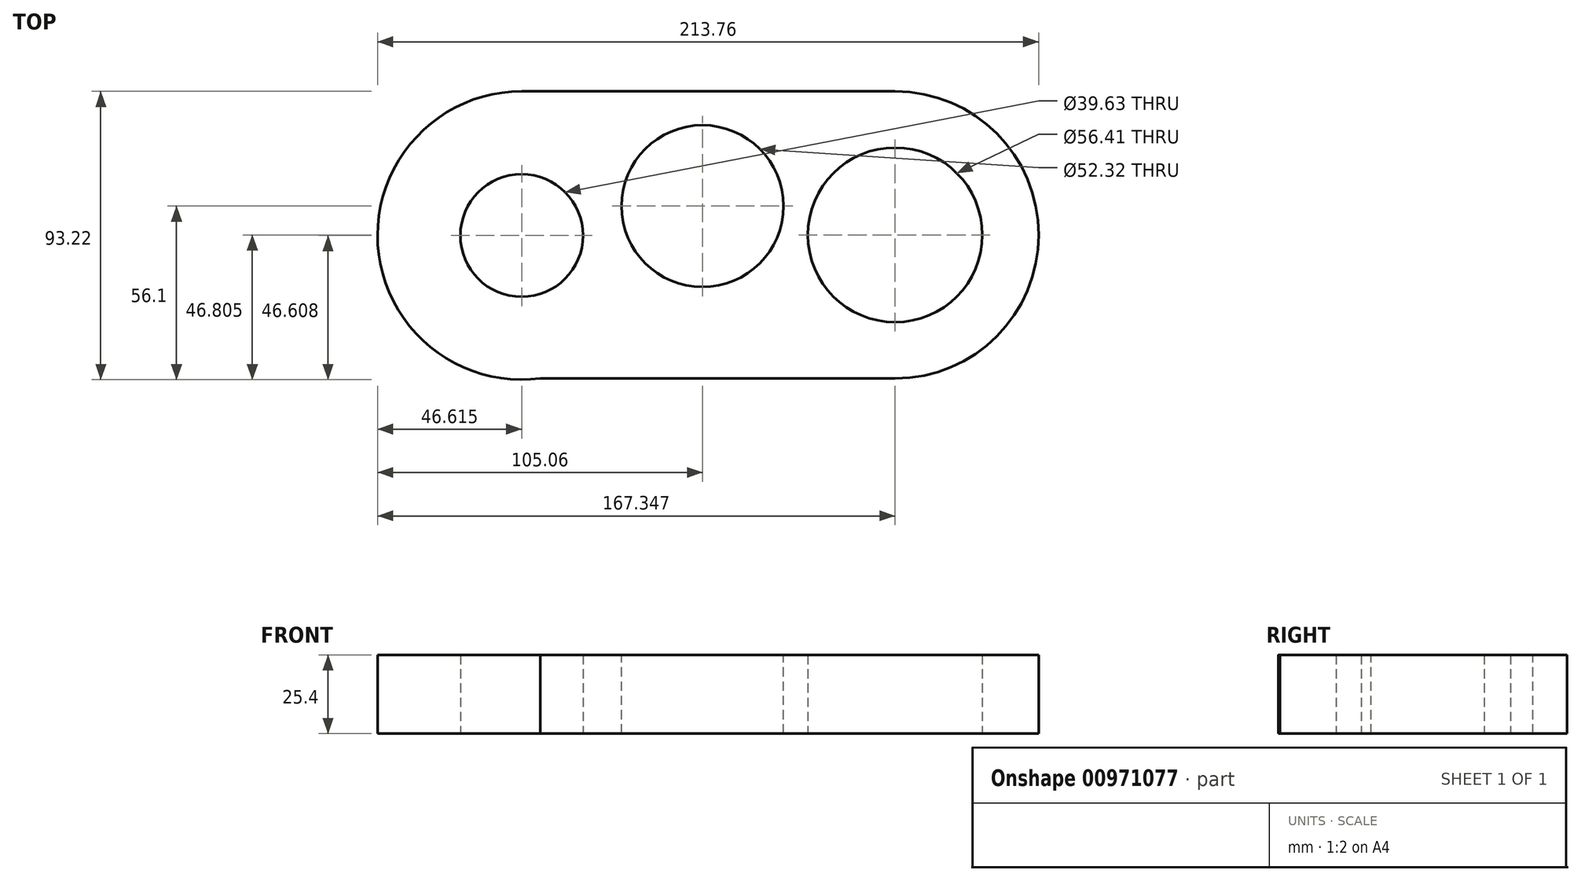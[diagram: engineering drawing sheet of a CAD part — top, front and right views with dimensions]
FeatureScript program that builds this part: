
annotation { "Feature Type Name" : "Feature", "Feature Type Description" : "" }
export const myFeature = defineFeature(function(context is Context, id is Id, definition is map)
    precondition{}
    {
        {
            var Q0;
            Q0=qCreatedBy(makeId("Top.planeOp"),FACE);
            var sketch = newSketch(context, id + "F0", { "sketchPlane" : qUnion([Q0])});
            skLineSegment(sketch, "E0", {"start": v(-58.45, 37.12) * mm, "end": v(62.29, 37.12) * mm});
            skLineSegment(sketch, "E1", {"start": v(-52.4, -55.7) * mm, "end": v(62.29, -55.7) * mm});
            skArc(sketch, "E2", {"start": v(-58.45, 37.12) * mm, "mid": v(-104.96, -12.52) * mm, "end": v(-52.4, -55.7) * mm});
            skArc(sketch, "E3", {"start": v(62.29, 37.12) * mm, "mid": v(108.7, -9.3) * mm, "end": v(62.29, -55.7) * mm});
            skCircle(sketch, "E4", {"center": v(-58.45, -9.5) * mm, "radius": 19.82 * mm});
            skCircle(sketch, "E5", {"center": v(62.29, -9.3) * mm, "radius": 28.2 * mm});
            skSolve(sketch);
        }
        {
            var Q0;
            Q0=makeQuery(id+"F0.imprint","IMPRINT",FACE,{"disambiguationData":[TD([[makeQuery(id+"F0.imprint","IMPRINT",EDGE,{"derivedFrom":sQuery(id+"F0.wireOp",EDGE,"E0")}),-1.0]])]});
            extrude(context, id + "F1", {"entities" : qUnion([Q0]), "depth" : 25.4 * mm, "offsetDistance" : 25.4 * mm});
        }
        {
            var Q0;
            Q0=makeQuery(id+"F1.opExtrude","CAP_FACE",FACE,{"disambiguationData":[OSD([sQuery(id+"F0.wireOp",EDGE,"E0"),sQuery(id+"F0.wireOp",EDGE,"E1"),sQuery(id+"F0.wireOp",EDGE,"E2"),sQuery(id+"F0.wireOp",EDGE,"E3"),sQuery(id+"F0.wireOp",EDGE,"E4"),sQuery(id+"F0.wireOp",EDGE,"E5")])],"isStart":false});
            var sketch = newSketch(context, id + "F2", { "sketchPlane" : qUnion([Q0])});
            skCircle(sketch, "E6", {"center": v(0, 0) * mm, "radius": 26.16 * mm});
            skSolve(sketch);
        }
        {
            var Q0;
            Q0=makeQuery(id+"F2.imprint","IMPRINT",FACE,{"disambiguationData":[TD([[makeQuery(id+"F2.imprint","IMPRINT",EDGE,{"derivedFrom":sQuery(id+"F2.wireOp",EDGE,"E6")}),1.0]])]});
            extrude(context, id + "F3", {"entities" : qUnion([Q0]), "operationType" : NewBodyOperationType.REMOVE, "oppositeDirection" : true, "depth" : 95.9 * mm, "offsetDistance" : 25.4 * mm});
        }
    });
